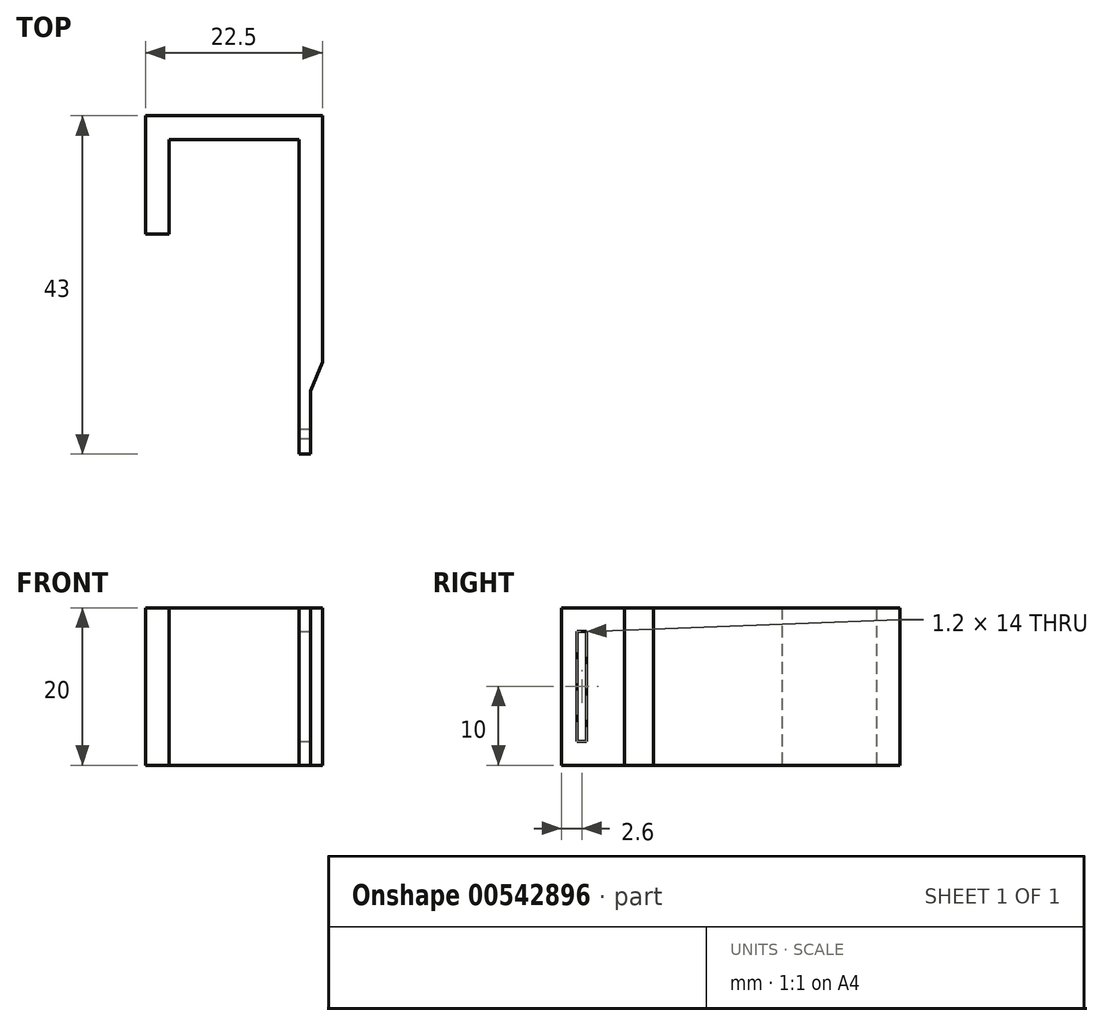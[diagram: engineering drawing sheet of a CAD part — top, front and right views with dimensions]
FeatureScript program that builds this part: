
annotation { "Feature Type Name" : "Feature", "Feature Type Description" : "" }
export const myFeature = defineFeature(function(context is Context, id is Id, definition is map)
    precondition{}
    {
        {
            var Q0;
            Q0=qCreatedBy(makeId("Top.planeOp"),FACE);
            var sketch = newSketch(context, id + "F0", { "sketchPlane" : qUnion([Q0])});
            skLineSegment(sketch, "E0", {"start": v(-8.25, 0) * mm, "end": v(8.25, 0) * mm});
            skLineSegment(sketch, "E1", {"start": v(8.25, 0) * mm, "end": v(8.25, -40) * mm});
            skLineSegment(sketch, "E2", {"start": v(8.25, -40) * mm, "end": v(9.75, -40) * mm});
            skLineSegment(sketch, "E3", {"start": v(11.25, -28.3) * mm, "end": v(11.25, 3) * mm});
            skLineSegment(sketch, "E4", {"start": v(11.25, 3) * mm, "end": v(-11.25, 3) * mm});
            skLineSegment(sketch, "E5", {"start": v(-11.25, 3) * mm, "end": v(-11.25, -12) * mm});
            skLineSegment(sketch, "E6", {"start": v(-11.25, -12) * mm, "end": v(-8.25, -12) * mm});
            skLineSegment(sketch, "E7", {"start": v(-8.25, -12) * mm, "end": v(-8.25, 0) * mm});
            skPoint(sketch, "E8", {"position": v(0, 0) * mm});
            skLineSegment(sketch, "E9", {"start": v(9.75, -40) * mm, "end": v(9.75, -32) * mm});
            skLineSegment(sketch, "E10", {"start": v(9.75, -32) * mm, "end": v(11.25, -28.3) * mm});
            skSolve(sketch);
        }
        {
            var Q0;
            Q0 = qSketchRegion(id + "F0", true);
            extrude(context, id + "F1", {"entities" : qUnion([Q0]), "depth" : 20 * mm, "offsetDistance" : 25 * mm});
        }
        {
            var Q0;
            Q0=makeQuery(id+"F1.opExtrude","SWEPT_FACE",FACE,{"disambiguationData":[OSD([sQuery(id+"F0.wireOp",EDGE,"E9")])]});
            var sketch = newSketch(context, id + "F2", { "sketchPlane" : qUnion([Q0])});
            skLineSegment(sketch, "E11.bottom", {"start": v(-36.8, 17) * mm, "end": v(-38, 17) * mm});
            skLineSegment(sketch, "E11.top", {"start": v(-36.8, 3) * mm, "end": v(-38, 3) * mm});
            skLineSegment(sketch, "E11.left", {"start": v(-36.8, 17) * mm, "end": v(-36.8, 3) * mm});
            skLineSegment(sketch, "E11.right", {"start": v(-38, 17) * mm, "end": v(-38, 3) * mm});
            skSolve(sketch);
        }
        {
            var Q0;
            Q0 = qSketchRegion(id + "F2", true);
            extrude(context, id + "F3", {"entities" : qUnion([Q0]), "operationType" : NewBodyOperationType.REMOVE, "oppositeDirection" : true, "depth" : 5 * mm, "offsetDistance" : 25 * mm});
        }
    });
